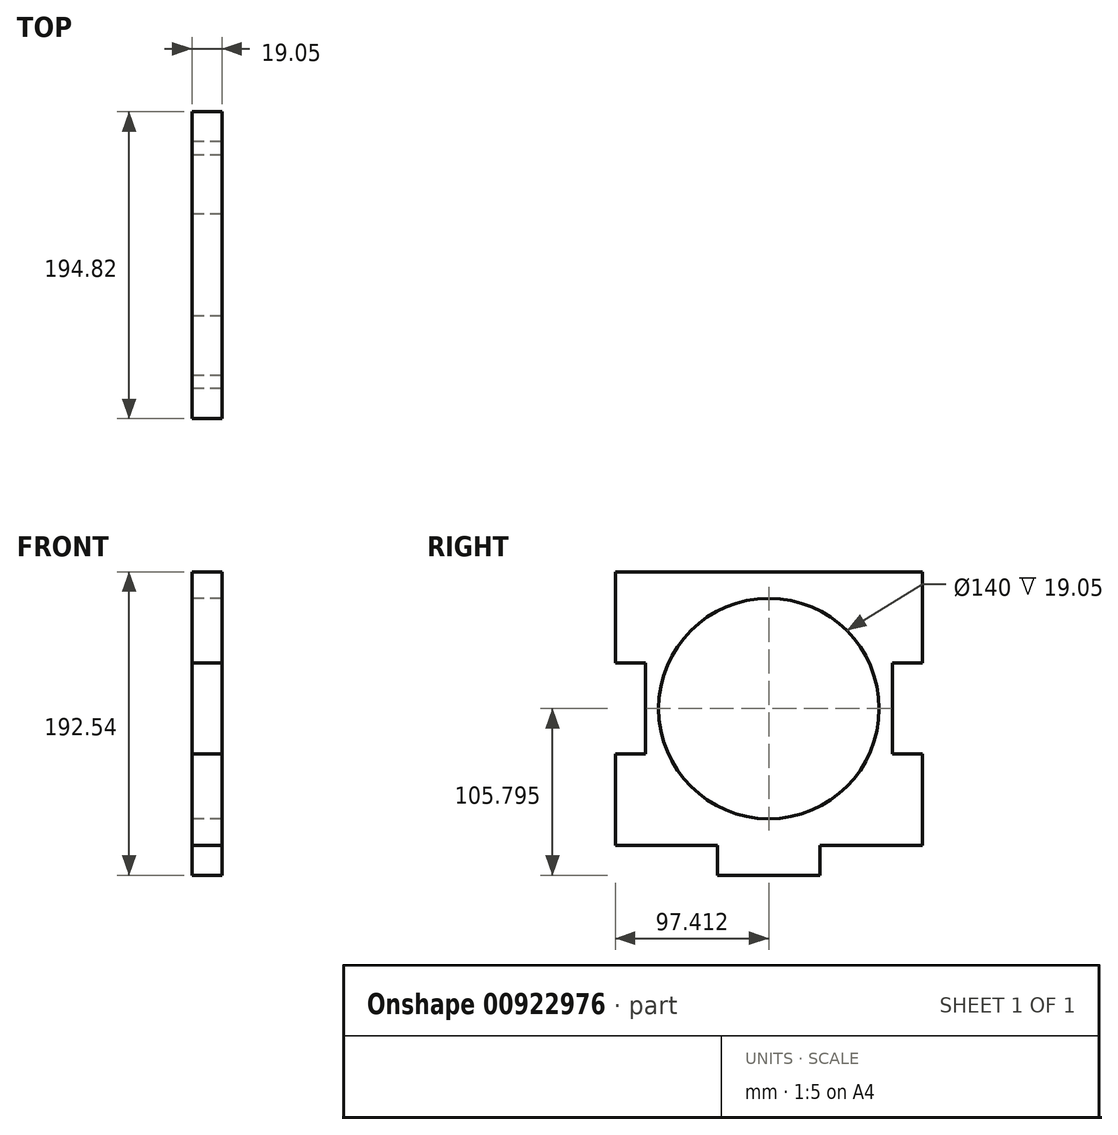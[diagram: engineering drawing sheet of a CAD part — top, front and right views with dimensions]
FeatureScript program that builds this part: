
annotation { "Feature Type Name" : "Feature", "Feature Type Description" : "" }
export const myFeature = defineFeature(function(context is Context, id is Id, definition is map)
    precondition{}
    {
        {
            var Q0;
            Q0=qCreatedBy(makeId("Right.planeOp"),FACE);
            var sketch = newSketch(context, id + "F0", { "sketchPlane" : qUnion([Q0])});
            skLineSegment(sketch, "E0.bottom", {"start": v(110.44, 96.27) * mm, "end": v(-84.38, 96.27) * mm});
            skLineSegment(sketch, "E0.left", {"start": v(110.44, 96.27) * mm, "end": v(110.44, 38.44) * mm});
            skLineSegment(sketch, "E0.right", {"start": v(-84.38, 96.27) * mm, "end": v(-84.38, 38.44) * mm});
            skPoint(sketch, "E1", {"position": v(13.03, -96.27) * mm});
            skPoint(sketch, "E2", {"position": v(45.5, -96.27) * mm});
            skPoint(sketch, "E3", {"position": v(-19.44, -96.27) * mm});
            skPoint(sketch, "E4", {"position": v(110.44, -77.22) * mm});
            skLineSegment(sketch, "E5", {"start": v(-84.38, -77.22) * mm, "end": v(-19.44, -77.22) * mm});
            skLineSegment(sketch, "E6", {"start": v(45.5, -96.27) * mm, "end": v(45.5, -77.22) * mm});
            skLineSegment(sketch, "E7", {"start": v(45.5, -96.27) * mm, "end": v(-19.44, -96.27) * mm});
            skLineSegment(sketch, "E8", {"start": v(-19.44, -96.27) * mm, "end": v(-19.44, -77.22) * mm});
            skLineSegment(sketch, "E9.trimOffspring", {"start": v(45.5, -77.22) * mm, "end": v(110.44, -77.22) * mm});
            skPoint(sketch, "E10", {"position": v(110.44, -19.39) * mm});
            skPoint(sketch, "E11", {"position": v(110.44, 38.44) * mm});
            skLineSegment(sketch, "E12", {"start": v(110.44, -19.39) * mm, "end": v(91.4, -19.39) * mm});
            skLineSegment(sketch, "E13", {"start": v(91.4, -19.39) * mm, "end": v(91.4, 38.44) * mm});
            skLineSegment(sketch, "E14", {"start": v(91.4, 38.44) * mm, "end": v(110.44, 38.44) * mm});
            skLineSegment(sketch, "E15.trimOffspring", {"start": v(110.44, -19.39) * mm, "end": v(110.44, -77.22) * mm});
            skPoint(sketch, "E16", {"position": v(-84.38, 38.44) * mm});
            skPoint(sketch, "E17", {"position": v(-84.38, -19.39) * mm});
            skLineSegment(sketch, "E18", {"start": v(-84.38, -19.39) * mm, "end": v(-65.33, -19.39) * mm});
            skLineSegment(sketch, "E19", {"start": v(-65.33, -19.39) * mm, "end": v(-65.33, 38.44) * mm});
            skLineSegment(sketch, "E20", {"start": v(-65.33, 38.44) * mm, "end": v(-84.38, 38.44) * mm});
            skLineSegment(sketch, "E21.trimOffspring", {"start": v(-84.38, -19.39) * mm, "end": v(-84.38, -77.22) * mm});
            skPoint(sketch, "E22", {"position": v(13.03, 9.52) * mm});
            skPoint(sketch, "E22.positionSnap0", {"position": v(13.03, 96.27) * mm});
            skPoint(sketch, "E22.positionSnap1", {"position": v(-65.33, 9.52) * mm});
            skSolve(sketch);
        }
        {
            var Q0;
            Q0=makeQuery(id+"F0.imprint","IMPRINT",FACE,{"disambiguationData":[TD([[makeQuery(id+"F0.imprint","IMPRINT",EDGE,{"derivedFrom":sQuery(id+"F0.wireOp",EDGE,"E0.bottom")}),1.0]])]});
            extrude(context, id + "F1", {"entities" : qUnion([Q0]), "depth" : 19.05 * mm, "offsetDistance" : 25.4 * mm});
        }
        {
            var Q0;
            Q0=sQuery(id+"F0.wireOp",VERTEX,"E22");
            var Q1;
            Q1=makeQuery(id+"F1.opExtrude","SWEPT_BODY",BODY,{"disambiguationData":[OSD([sQuery(id+"F0.wireOp",EDGE,"E0.bottom"),sQuery(id+"F0.wireOp",EDGE,"E0.left"),sQuery(id+"F0.wireOp",EDGE,"E0.right"),sQuery(id+"F0.wireOp",EDGE,"E5"),sQuery(id+"F0.wireOp",EDGE,"E6"),sQuery(id+"F0.wireOp",EDGE,"E7"),sQuery(id+"F0.wireOp",EDGE,"E8"),sQuery(id+"F0.wireOp",EDGE,"E9.trimOffspring"),sQuery(id+"F0.wireOp",EDGE,"E12"),sQuery(id+"F0.wireOp",EDGE,"E13"),sQuery(id+"F0.wireOp",EDGE,"E14"),sQuery(id+"F0.wireOp",EDGE,"E15.trimOffspring"),sQuery(id+"F0.wireOp",EDGE,"E18"),sQuery(id+"F0.wireOp",EDGE,"E19"),sQuery(id+"F0.wireOp",EDGE,"E20"),sQuery(id+"F0.wireOp",EDGE,"E21.trimOffspring")])]});
            hole(context, id + "F2", {"style" : HoleStyle.SIMPLE, "endStyle" : HoleEndStyle.BLIND, "oppositeDirection" : true, "holeDiameter" : 140 * mm, "majorDiameter" : 6.35 * mm, "holeDepth" : 50.8 * mm, "isTappedThrough" : true, "tappedDepth" : 12.7 * mm, "tapClearance" : 3, "locations" : qUnion([Q0]), "scope" : qUnion([Q1])});
        }
    });
